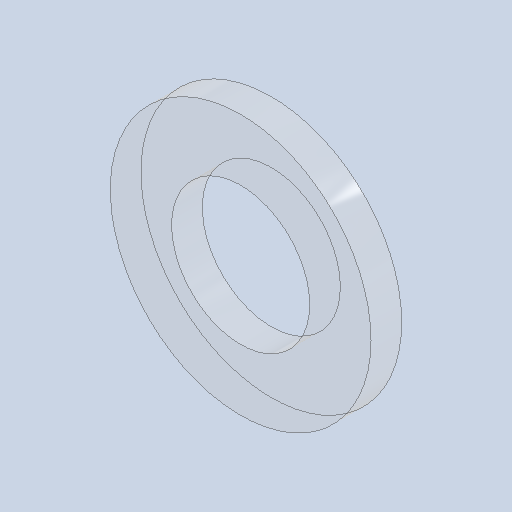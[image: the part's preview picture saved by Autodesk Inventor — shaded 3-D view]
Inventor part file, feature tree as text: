
AUTODESK INVENTOR PART (.ipt)
format: ipt  version: 2022 (Build 260153000, 153)  size: 113,152 bytes
history: native  units: mm
features: extrude x1, sketch x1
ambient origin geometry x8: Origin, YZ Plane, XZ Plane, XY Plane, X Axis, Y Axis, Z Axis, Center Point
bodies: Solid1 (feature_tree)
feature tree (2):
  extrude  "Extrusion1"  Depth=2.0mm
  sketch  "Sketch1"  dims[d0=17.0mm d1=9.0mm d2=2.0mm d3=0.0mm]
